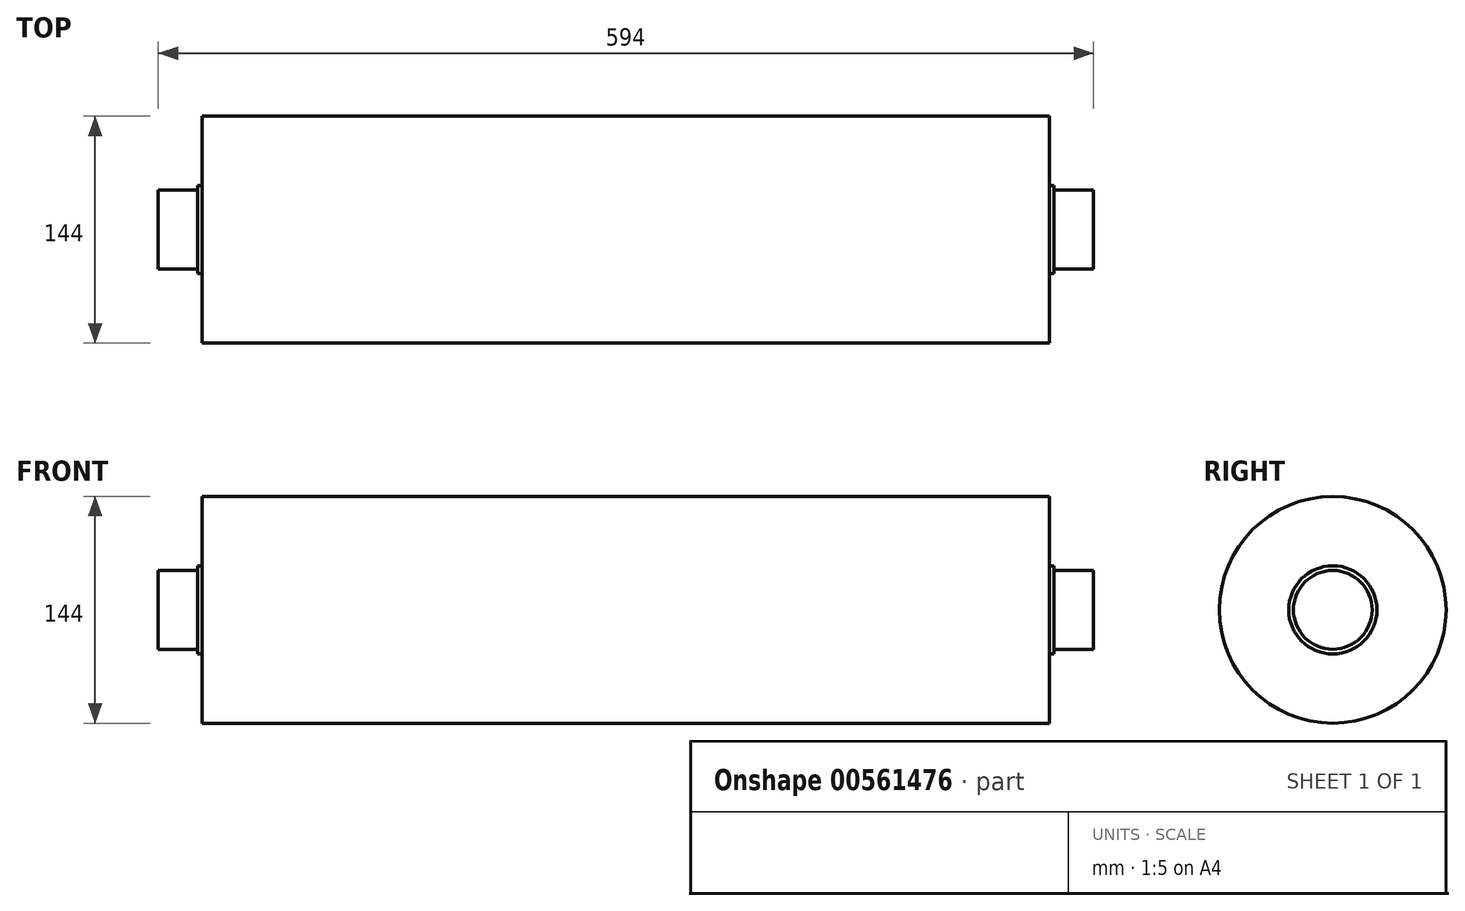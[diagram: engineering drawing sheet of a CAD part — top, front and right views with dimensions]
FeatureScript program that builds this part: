
annotation { "Feature Type Name" : "Feature", "Feature Type Description" : "" }
export const myFeature = defineFeature(function(context is Context, id is Id, definition is map)
    precondition{}
    {
        {
            var Q0;
            Q0=qCreatedBy(makeId("Front.planeOp"),FACE);
            var sketch = newSketch(context, id + "F0", { "sketchPlane" : qUnion([Q0])});
            skLineSegment(sketch, "E0", {"start": v(-297, 0) * mm, "end": v(0, 0) * mm});
            skLineSegment(sketch, "E1", {"start": v(0, 0) * mm, "end": v(297, 0) * mm});
            skLineSegment(sketch, "E2", {"start": v(297, 0) * mm, "end": v(297, 25) * mm});
            skLineSegment(sketch, "E3", {"start": v(297, 25) * mm, "end": v(272, 25) * mm});
            skLineSegment(sketch, "E4", {"start": v(272, 25) * mm, "end": v(272, 28) * mm});
            skLineSegment(sketch, "E5", {"start": v(272, 28) * mm, "end": v(269, 28) * mm});
            skLineSegment(sketch, "E6", {"start": v(269, 28) * mm, "end": v(269, 72) * mm});
            skLineSegment(sketch, "E7", {"start": v(269, 72) * mm, "end": v(-269, 72) * mm});
            skLineSegment(sketch, "E8", {"start": v(-269, 72) * mm, "end": v(-269, 28) * mm});
            skLineSegment(sketch, "E9", {"start": v(-269, 28) * mm, "end": v(-272, 28) * mm});
            skLineSegment(sketch, "E10", {"start": v(-272, 28) * mm, "end": v(-272, 25) * mm});
            skLineSegment(sketch, "E11", {"start": v(-272, 25) * mm, "end": v(-297, 25) * mm});
            skLineSegment(sketch, "E12", {"start": v(-297, 25) * mm, "end": v(-297, 0) * mm});
            skLineSegment(sketch, "E13", {"start": v(-315.33, 0) * mm, "end": v(313.4, 0) * mm, "construction": true});
            skSolve(sketch);
        }
        {
            var Q0;
            Q0=makeQuery(id+"F0.imprint","IMPRINT",FACE,{"disambiguationData":[TD([[makeQuery(id+"F0.imprint","IMPRINT",EDGE,{"derivedFrom":sQuery(id+"F0.wireOp",EDGE,"E0")}),1.0]])]});
            var Q1;
            Q1=sQuery(id+"F0.wireOp",EDGE,"E13");
            revolve(context, id + "F1", {"entities" : qUnion([Q0]), "axis" : qUnion([Q1]), "revolveType" : RevolveType.FULL});
        }
    });
